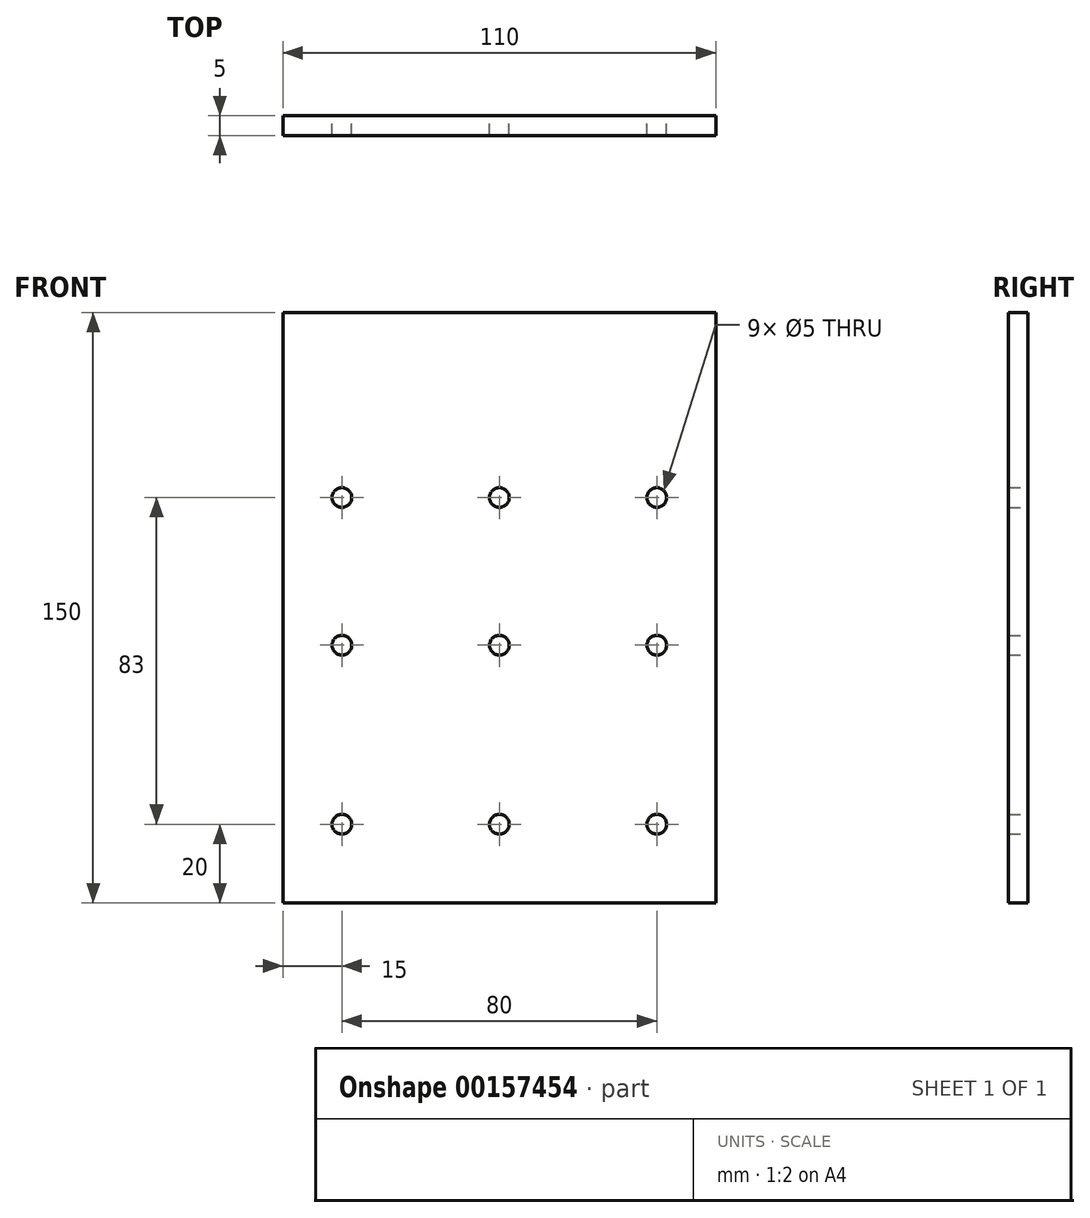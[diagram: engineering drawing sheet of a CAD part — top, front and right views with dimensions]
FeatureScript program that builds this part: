
annotation { "Feature Type Name" : "Feature", "Feature Type Description" : "" }
export const myFeature = defineFeature(function(context is Context, id is Id, definition is map)
    precondition{}
    {
        {
            var Q0;
            Q0=qCreatedBy(makeId("Front.planeOp"),FACE);
            var sketch = newSketch(context, id + "F0", { "sketchPlane" : qUnion([Q0])});
            skLineSegment(sketch, "E0.bottom", {"start": v(55, -75) * mm, "end": v(-55, -75) * mm});
            skLineSegment(sketch, "E0.top", {"start": v(55, 75) * mm, "end": v(0, 75) * mm});
            skLineSegment(sketch, "E0.left", {"start": v(55, -75) * mm, "end": v(55, 75) * mm});
            skLineSegment(sketch, "E0.right", {"start": v(-55, -75) * mm, "end": v(-55, 38.3) * mm});
            skPoint(sketch, "E0.middle", {"position": v(0, 0) * mm});
            skCircle(sketch, "E1", {"center": v(-40, 28) * mm, "radius": 2.5 * mm});
            skCircle(sketch, "E2", {"center": v(0, 28) * mm, "radius": 2.5 * mm});
            skCircle(sketch, "E3", {"center": v(-40, -55) * mm, "radius": 2.5 * mm});
            skCircle(sketch, "E4", {"center": v(0, -55) * mm, "radius": 2.5 * mm});
            skCircle(sketch, "E5", {"center": v(40, -55) * mm, "radius": 2.5 * mm});
            skCircle(sketch, "E6", {"center": v(40, 28) * mm, "radius": 2.5 * mm});
            skPoint(sketch, "E7.orphan", {"position": v(-55, 75) * mm});
            skLineSegment(sketch, "E8", {"start": v(0, 75) * mm, "end": v(-55, 75) * mm});
            skLineSegment(sketch, "E9", {"start": v(-55, 75) * mm, "end": v(-55, 38.3) * mm});
            skCircle(sketch, "E10", {"center": v(-40, -9.5) * mm, "radius": 2.5 * mm});
            skCircle(sketch, "E11", {"center": v(0, -9.5) * mm, "radius": 2.5 * mm});
            skCircle(sketch, "E12", {"center": v(40, -9.5) * mm, "radius": 2.5 * mm});
            skSolve(sketch);
        }
        {
            var Q0;
            Q0=makeQuery(id+"F0.imprint","IMPRINT",FACE,{"disambiguationData":[TD([[makeQuery(id+"F0.imprint","IMPRINT",EDGE,{"derivedFrom":sQuery(id+"F0.wireOp",EDGE,"E0.bottom")}),-1.0]])]});
            extrude(context, id + "F1", {"entities" : qUnion([Q0]), "depth" : 5 * mm});
        }
    });
